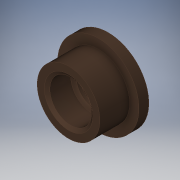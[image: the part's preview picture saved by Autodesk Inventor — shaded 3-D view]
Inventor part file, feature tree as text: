
AUTODESK INVENTOR PART (.ipt)
format: ipt  version: 2018 (Build 220112000, 112)  size: 163,840 bytes
history: native  units: mm
features: revolve x1, sketch x1
ambient origin geometry x8: Origin, YZ Plane, XZ Plane, XY Plane, X Axis, Y Axis, Z Axis, Center Point
bodies: Solid1 (feature_tree)
feature tree (2):
  revolve  "Revolution1"  [1 undecoded]
  sketch  "Sketch1"  dims[d0=28.5mm d1=27.0mm d2=19.0mm d3=3.0mm d4=2.0mm d5=21.0mm d6=3.0mm d7=2.0mm d8=3.0mm d17=3.0mm d18=5.5mm d19=4.0mm d20=10.0mm d21=3.0mm d22=6.0mm d23=5.0mm d24=3.0mm d25=8.5mm d26=90.0deg]
note: 1 required parameter value undecoded (feature->parameter linkage not recoverable at this tier; creation-order binding heuristic only, values carry confidence <= 0.55)
